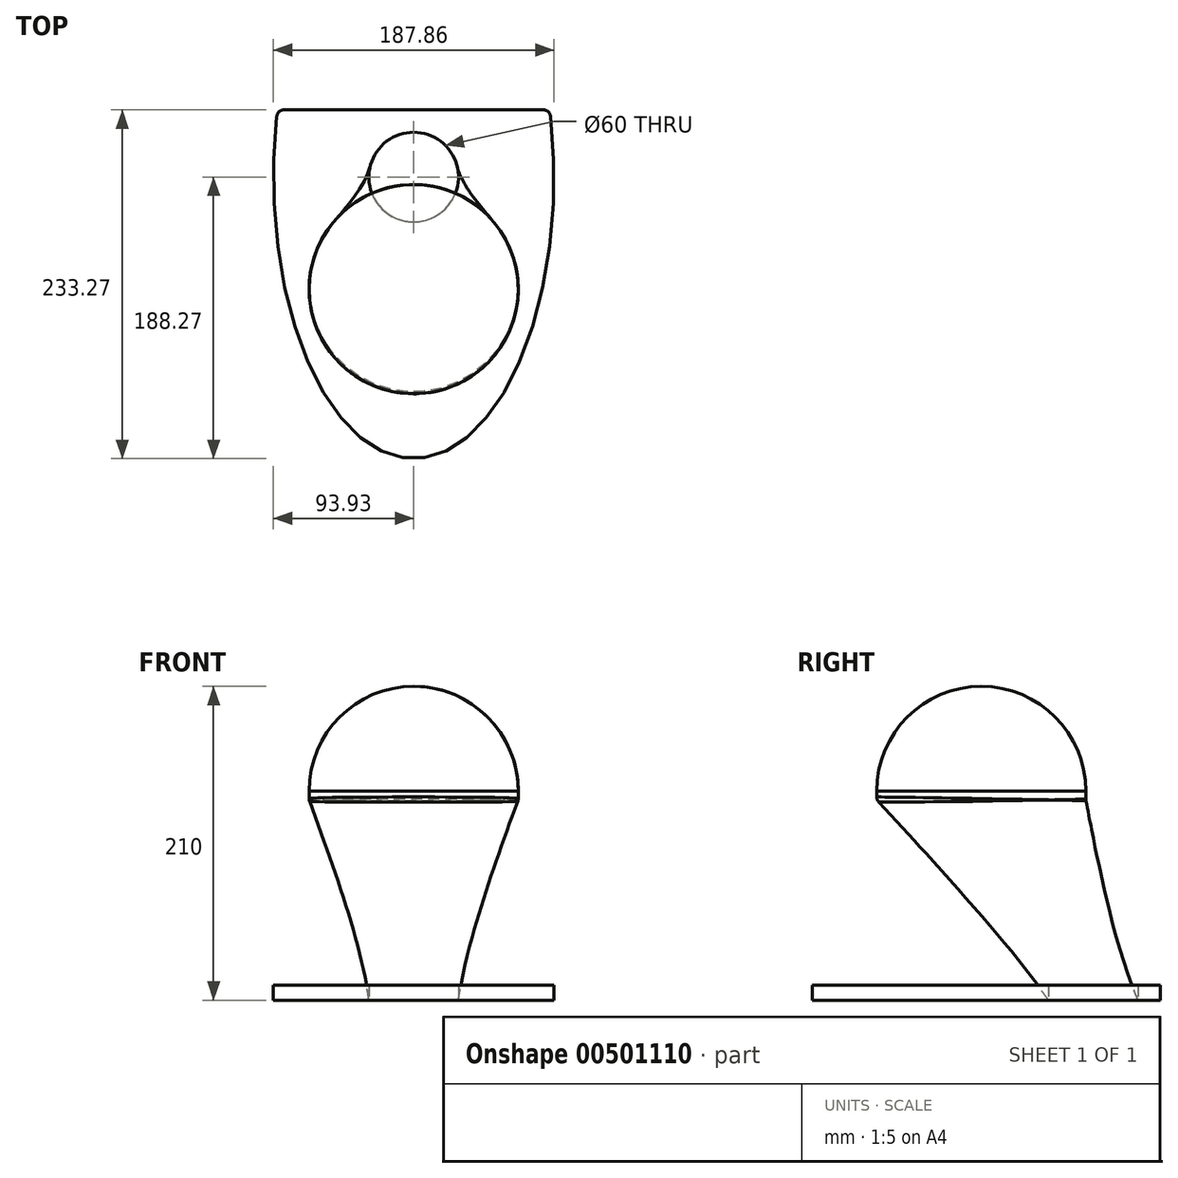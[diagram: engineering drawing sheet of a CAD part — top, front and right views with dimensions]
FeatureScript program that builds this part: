
annotation { "Feature Type Name" : "Feature", "Feature Type Description" : "" }
export const myFeature = defineFeature(function(context is Context, id is Id, definition is map)
    precondition{}
    {
        {
            var Q0;
            Q0=qCreatedBy(makeId("Front.planeOp"),FACE);
            var sketch = newSketch(context, id + "F0", { "sketchPlane" : qUnion([Q0])});
            skLineSegment(sketch, "E0", {"start": v(-70, 0) * mm, "end": v(0, 0) * mm});
            skLineSegment(sketch, "E1", {"start": v(0, 0) * mm, "end": v(0, 70) * mm});
            skLineSegment(sketch, "E2", {"start": v(0, 0) * mm, "end": v(70, 0) * mm, "construction": true});
            skArc(sketch, "E3", {"start": v(70, 0) * mm, "mid": v(0, 70) * mm, "end": v(-70, 0) * mm});
            skSolve(sketch);
        }
        {
            var Q0;
            Q0=makeQuery(id+"F0.imprint","IMPRINT",FACE,{"disambiguationData":[TD([[makeQuery(id+"F0.imprint","IMPRINT",EDGE,{"derivedFrom":sQuery(id+"F0.wireOp",EDGE,"E0")}),1.0]])]});
            var Q1;
            Q1=sQuery(id+"F0.wireOp",EDGE,"E1");
            revolve(context, id + "F1", {"entities" : qUnion([Q0]), "axis" : qUnion([Q1]), "revolveType" : RevolveType.FULL});
        }
        {
            var Q0;
            Q0=makeQuery(id+"F1.opRevolve","SWEPT_FACE",FACE,{"disambiguationData":[OSD([sQuery(id+"F0.wireOp",EDGE,"E0")])]});
            var sketch = newSketch(context, id + "F2", { "sketchPlane" : qUnion([Q0])});
            skCircle(sketch, "E4", {"center": v(0, 0) * mm, "radius": 70 * mm});
            skSolve(sketch);
        }
        {
            var Q0;
            Q0=makeQuery(id+"F2.imprint","IMPRINT",FACE,{"disambiguationData":[TD([[makeQuery(id+"F2.imprint","IMPRINT",EDGE,{"derivedFrom":sQuery(id+"F2.wireOp",EDGE,"E4")}),1.0]])]});
            extrude(context, id + "F3", {"entities" : qUnion([Q0]), "depth" : 6 * mm});
        }
        {
            var Q0;
            Q0=qCreatedBy(makeId("Top.planeOp"),FACE);
            cPlane(context, id + "F4", {"entities" : qUnion([Q0]), "cplaneType" : CPlaneType.OFFSET, "offset" : 140 * mm, "oppositeDirection" : true, "width" : 150 * mm, "height" : 150 * mm});
        }
        {
            var Q0;
            Q0=qCreatedBy(id+"F4.planeOp",FACE);
            var sketch = newSketch(context, id + "F5", { "sketchPlane" : qUnion([Q0])});
            skCircle(sketch, "E5", {"center": v(0, 75) * mm, "radius": 30 * mm});
            skSolve(sketch);
        }
        {
            var Q1;
            Q1=makeQuery(id+"F3.opExtrude","CAP_FACE",FACE,{"disambiguationData":[OSD([sQuery(id+"F2.wireOp",EDGE,"E4")])],"isStart":false});
            var Q2;
            Q2=makeQuery(id+"F5.imprint","IMPRINT",FACE,{"disambiguationData":[TD([[makeQuery(id+"F5.imprint","IMPRINT",EDGE,{"derivedFrom":sQuery(id+"F5.wireOp",EDGE,"E5")}),1.0]])]});
            loft(context, id + "F6", {"operationType" : NewBodyOperationType.ADD, "sheetProfilesArray" : [{ "sheetProfileEntities" : qUnion([Q1]) }, { "sheetProfileEntities" : qUnion([Q2]) }]});
        }
        {
            var Q0;
            Q0=makeQuery(id+"F6.opLoft","CAP_FACE",FACE,{"disambiguationData":[OSD([makeQuery(id+"F5.imprint","IMPRINT",FACE,{"disambiguationData":[TD([[makeQuery(id+"F5.imprint","IMPRINT",EDGE,{"derivedFrom":sQuery(id+"F5.wireOp",EDGE,"E5")}),1.0]])]})])],"isStart":true});
            var sketch = newSketch(context, id + "F7", { "sketchPlane" : qUnion([Q0])});
            skEllipticalArc(sketch, "E6", {});
            skLineSegment(sketch, "E7", {"start": v(86.75, -120) * mm, "end": v(-86.75, -120) * mm});
            skPoint(sketch, "E8.visualSharp", {"position": v(91.2, -120) * mm});
            skArc(sketch, "E8.filletArc", {"start": v(86.75, -120) * mm, "mid": v(90.09, -118.72) * mm, "end": v(91.72, -115.55) * mm});
            skPoint(sketch, "E9.visualSharp", {"position": v(-91.2, -120) * mm});
            skArc(sketch, "E9.filletArc", {"start": v(-91.72, -115.55) * mm, "mid": v(-90.09, -118.72) * mm, "end": v(-86.75, -120) * mm});
            const initialGuessF7  = {"E6": [0, -0.075, 0, 1, 0.18827325893347996, 0.0939262089381113, 4.495326990537996, 1.7878583166597728]};
            skSetInitialGuess(sketch, initialGuessF7);
            skSolve(sketch);
        }
        {
            var Q0;
            Q0=makeQuery(id+"F7.imprint","IMPRINT",FACE,{"disambiguationData":[TD([[makeQuery(id+"F7.imprint","IMPRINT",EDGE,{"derivedFrom":sQuery(id+"F7.wireOp",EDGE,"E6")}),1.0]])]});
            extrude(context, id + "F8", {"entities" : qUnion([Q0]), "oppositeDirection" : true, "depth" : 10 * mm});
        }
        {
            var Q0;
            {var subQ0=sQuery(id+"F2.wireOp",EDGE,"E4");Q0=makeQuery(id+"F6.boolean.opBoolean","MERGE",EDGE,{"derivedFrom":[makeQuery(id+"F3.opExtrude","CAP_EDGE",EDGE,{"disambiguationData":[OSD([subQ0])],"isStart":false}),makeQuery(id+"F6.opLoft","MID_CAP_EDGE",EDGE,{"disambiguationData":[OSD([subQ0])],"capPos":0.0})]});}
            fillet(context, id + "F9", {"entities" : qUnion([Q0]), "radius" : 5 * mm, "tangentPropagation" : true, "allowEdgeOverflow" : false});
        }
    });
